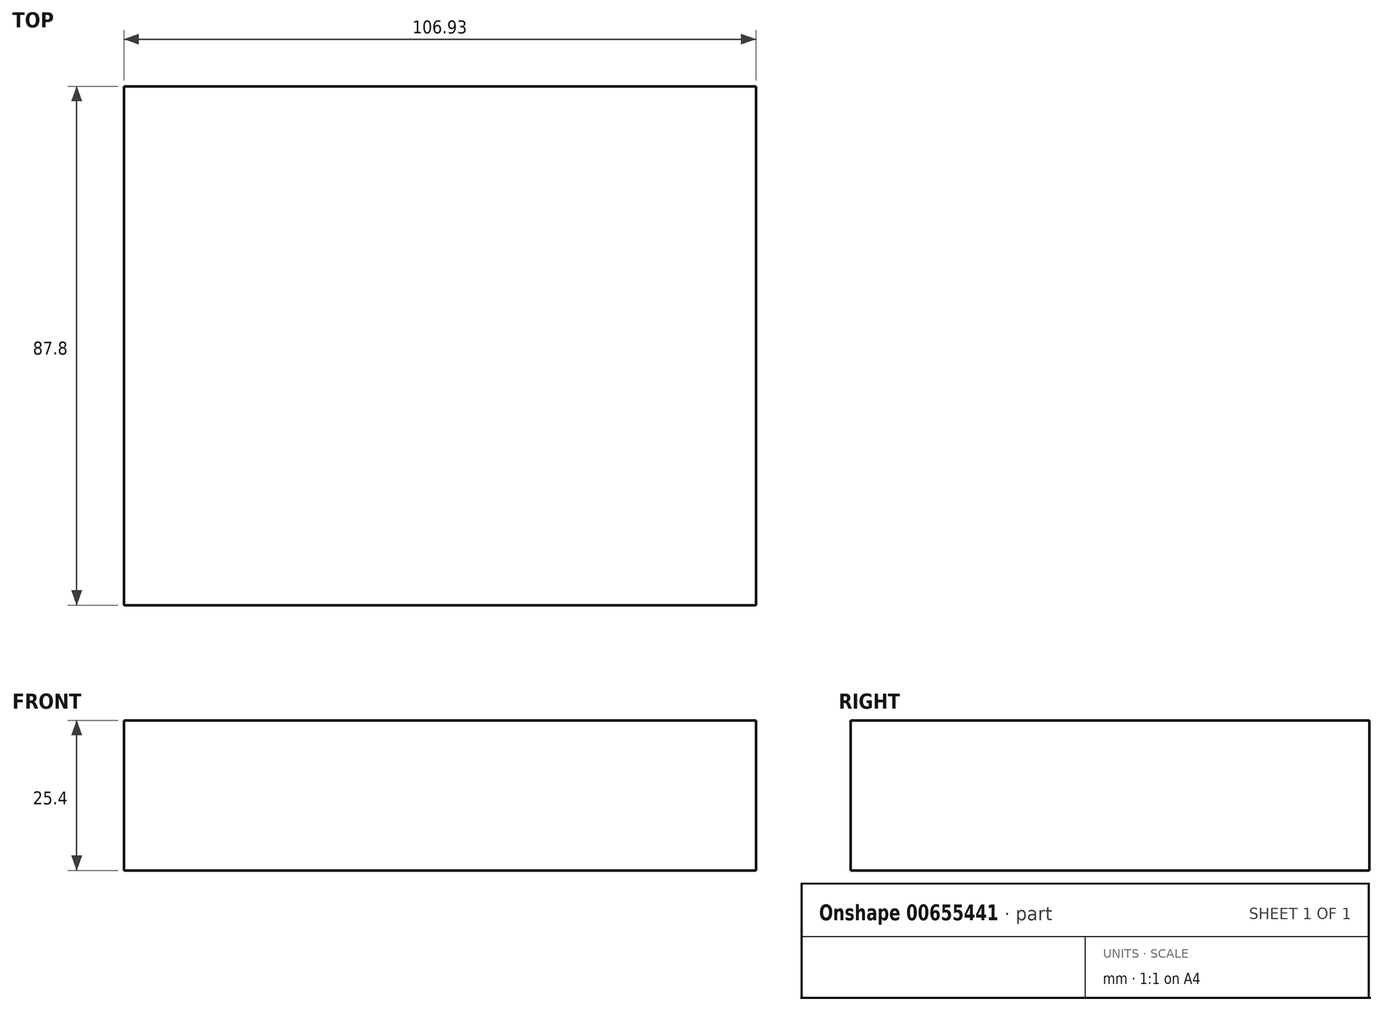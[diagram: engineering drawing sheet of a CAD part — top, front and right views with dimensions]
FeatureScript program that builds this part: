
annotation { "Feature Type Name" : "Feature", "Feature Type Description" : "" }
export const myFeature = defineFeature(function(context is Context, id is Id, definition is map)
    precondition{}
    {
        {
            var Q0;
            Q0=qCreatedBy(makeId("Top.planeOp"),FACE);
            var sketch = newSketch(context, id + "F0", { "sketchPlane" : qUnion([Q0])});
            skLineSegment(sketch, "E0.bottom", {"start": v(0, 0) * mm, "end": v(81.53, 0) * mm});
            skLineSegment(sketch, "E0.top", {"start": v(0, -62.4) * mm, "end": v(81.53, -62.4) * mm});
            skLineSegment(sketch, "E0.left", {"start": v(0, 0) * mm, "end": v(0, -62.4) * mm});
            skLineSegment(sketch, "E0.right", {"start": v(81.53, 0) * mm, "end": v(81.53, -62.4) * mm});
            skSolve(sketch);
        }
        {
            var Q0;
            Q0 = qSketchRegion(id + "F0", true);
            extrude(context, id + "F1", {"entities" : qUnion([Q0]), "depth" : 25.4 * mm, "offsetDistance" : 25.4 * mm});
        }
        {
            var Q0;
            Q0=makeQuery(id+"F1.opExtrude","SWEPT_FACE",FACE,{"disambiguationData":[OSD([sQuery(id+"F0.wireOp",EDGE,"E0.right")])]});
            extrude(context, id + "F2", {"entities" : qUnion([Q0]), "operationType" : NewBodyOperationType.ADD, "depth" : 25.4 * mm, "offsetDistance" : 25.4 * mm});
        }
        {
            var Q0;
            {var subQ0=sQuery(id+"F0.wireOp",EDGE,"E0.top");Q0=makeQuery(id+"F2.boolean.opBoolean","MERGE",FACE,{"derivedFrom":[makeQuery(id+"F1.opExtrude","SWEPT_FACE",FACE,{"disambiguationData":[OSD([subQ0])]}),makeQuery(id+"F2.opExtrude","SWEPT_FACE",FACE,{"disambiguationData":[OSD([subQ0,sQuery(id+"F0.wireOp",EDGE,"E0.right")])]})]});}
            extrude(context, id + "F3", {"entities" : qUnion([Q0]), "operationType" : NewBodyOperationType.ADD, "depth" : 25.4 * mm, "offsetDistance" : 25.4 * mm});
        }
    });
